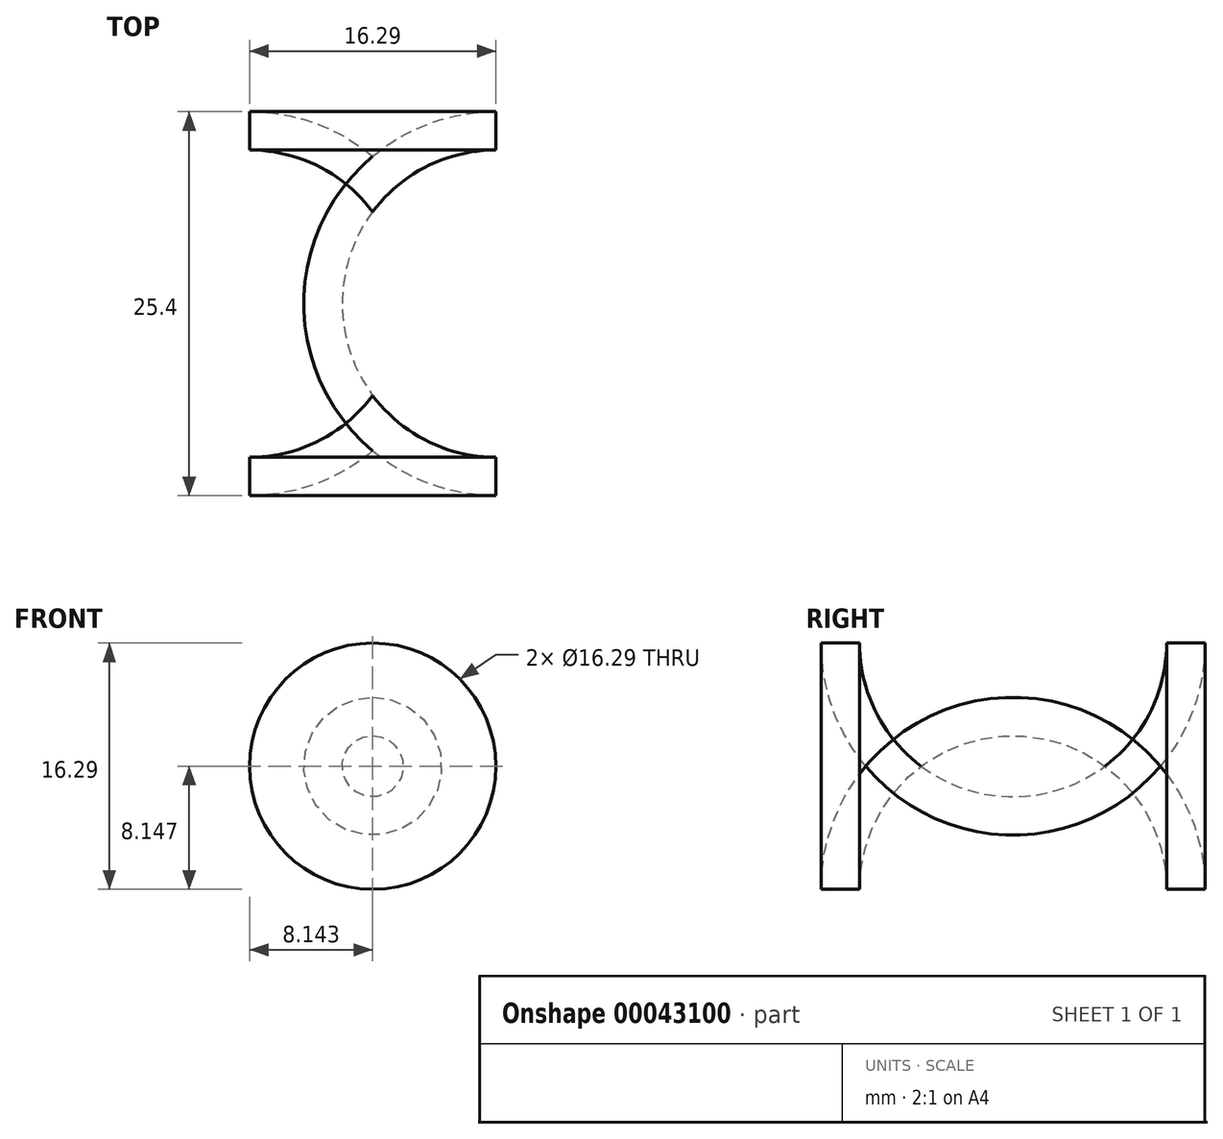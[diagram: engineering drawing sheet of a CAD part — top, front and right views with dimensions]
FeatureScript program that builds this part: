
annotation { "Feature Type Name" : "Feature", "Feature Type Description" : "" }
export const myFeature = defineFeature(function(context is Context, id is Id, definition is map)
    precondition{}
    {
        {
            var Q0;
            Q0=qCreatedBy(makeId("Front.planeOp"),FACE);
            var sketch = newSketch(context, id + "F0", { "sketchPlane" : qUnion([Q0])});
            skCircle(sketch, "E0", {"center": v(-29.68, 16.45) * mm, "radius": 20.84 * mm});
            skSolve(sketch);
        }
        {
            var Q0;
            Q0=makeQuery(id+"F0.imprint","IMPRINT",FACE,{"disambiguationData":[TD([[makeQuery(id+"F0.imprint","IMPRINT",EDGE,{"derivedFrom":sQuery(id+"F0.wireOp",EDGE,"E0")}),1.0]])]});
            extrude(context, id + "F1", {"entities" : qUnion([Q0]), "depth" : 25.4 * mm});
        }
        {
            var Q0;
            Q0=makeQuery(id+"F1.opExtrude","CAP_FACE",FACE,{"disambiguationData":[OSD([sQuery(id+"F0.wireOp",EDGE,"E0")])],"isStart":false});
            var Q1;
            Q1=makeQuery(id+"F1.opExtrude","SWEPT_FACE",FACE,{"disambiguationData":[OSD([sQuery(id+"F0.wireOp",EDGE,"E0")])]});
            fillet(context, id + "F2", {"entities" : qUnion([Q0, Q1]), "radius" : 12.7 * mm, "tangentPropagation" : true, "allowEdgeOverflow" : false});
        }
        {
            var Q0;
            Q0=makeQuery(id+"F1.opExtrude","CAP_FACE",FACE,{"disambiguationData":[OSD([sQuery(id+"F0.wireOp",EDGE,"E0")])],"isStart":true});
            shell(context, id + "F3", {"entities" : qUnion([Q0]), "thickness" : 2.54 * mm});
        }
        {
            var Q0;
            {var subQ0=sQuery(id+"F0.wireOp",EDGE,"E0");Q0=makeQuery(id+"F3.opShell","OFFSET_FACE",FACE,{"disambiguationData":[OSD([subQ0]),TDD([makeQuery(id+"F1.opExtrude","CAP_FACE",FACE,{"disambiguationData":[OSD([subQ0])],"isStart":false})])]});}
            var sketch = newSketch(context, id + "F4", { "sketchPlane" : qUnion([Q0])});
            skCircle(sketch, "E1.0", {"center": v(29.68, 16.45) * mm, "radius": 8.15 * mm});
            skSolve(sketch);
        }
        {
            var Q0;
            {var subQ0=sQuery(id+"F0.wireOp",EDGE,"E0");Q0=makeQuery(id+"F4.imprint","IMPRINT",FACE,{"disambiguationData":[TD([[makeQuery(id+"F4.imprint","IMPRINT",EDGE,{"derivedFrom":makeQuery(id+"F3.opShell","OFFSET_EDGE",EDGE,{"disambiguationData":[OSD([subQ0]),TDD([makeQuery(id+"F2.opFillet","BLEND_EDGE",EDGE,{"blendedFrom":[makeQuery(id+"F1.opExtrude","CAP_EDGE",EDGE,{"disambiguationData":[OSD([subQ0])],"isStart":false}),makeQuery(id+"F1.opExtrude","CAP_FACE",FACE,{"disambiguationData":[OSD([subQ0])],"isStart":false})],"blendedInto":[makeQuery(id+"F1.opExtrude","CAP_FACE",FACE,{"disambiguationData":[OSD([subQ0])],"isStart":false})]})])]})}),-1.0]])]});}
            extrude(context, id + "F5", {"entities" : qUnion([Q0]), "operationType" : NewBodyOperationType.REMOVE, "oppositeDirection" : true, "depth" : 25.4 * mm});
        }
    });
